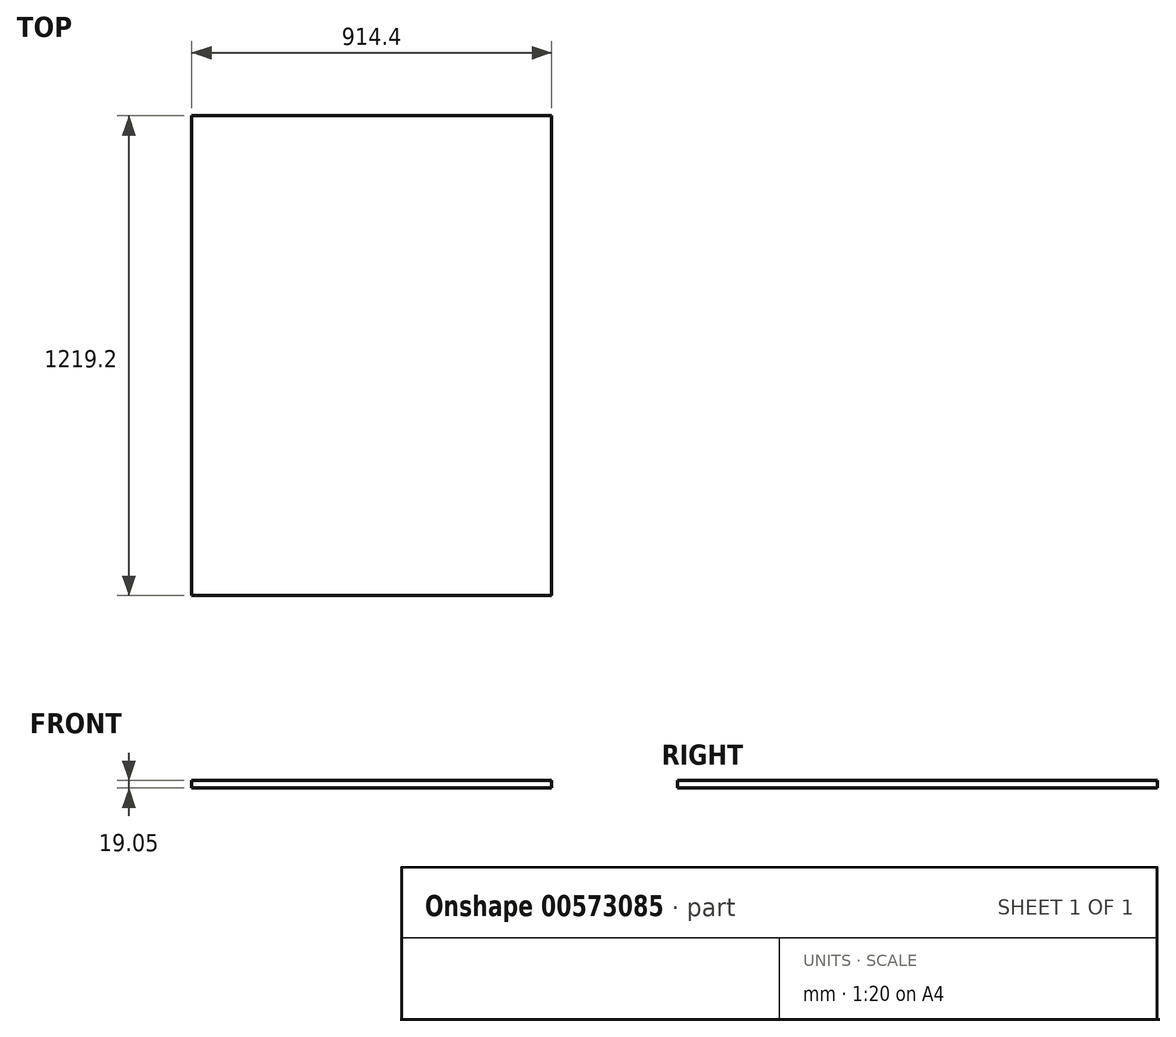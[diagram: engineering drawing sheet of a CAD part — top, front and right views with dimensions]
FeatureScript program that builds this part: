
annotation { "Feature Type Name" : "Feature", "Feature Type Description" : "" }
export const myFeature = defineFeature(function(context is Context, id is Id, definition is map)
    precondition{}
    {
        {
            var Q0;
            Q0=qCreatedBy(makeId("Top.planeOp"),FACE);
            var sketch = newSketch(context, id + "F0", { "sketchPlane" : qUnion([Q0])});
            skLineSegment(sketch, "E0.bottom", {"start": v(457.2, 609.6) * mm, "end": v(-457.2, 609.6) * mm});
            skLineSegment(sketch, "E0.top", {"start": v(457.2, -609.6) * mm, "end": v(-457.2, -609.6) * mm});
            skLineSegment(sketch, "E0.left", {"start": v(457.2, 609.6) * mm, "end": v(457.2, -609.6) * mm});
            skLineSegment(sketch, "E0.right", {"start": v(-457.2, 609.6) * mm, "end": v(-457.2, -609.6) * mm});
            skPoint(sketch, "E0.middle", {"position": v(0, 0) * mm});
            skSolve(sketch);
        }
        {
            var Q0;
            Q0=makeQuery(id+"F0.imprint","IMPRINT",FACE,{"disambiguationData":[TD([[makeQuery(id+"F0.imprint","IMPRINT",EDGE,{"derivedFrom":sQuery(id+"F0.wireOp",EDGE,"E0.bottom")}),1.0]])]});
            extrude(context, id + "F1", {"entities" : qUnion([Q0]), "depth" : 19.05 * mm, "offsetDistance" : 25.4 * mm});
        }
    });
